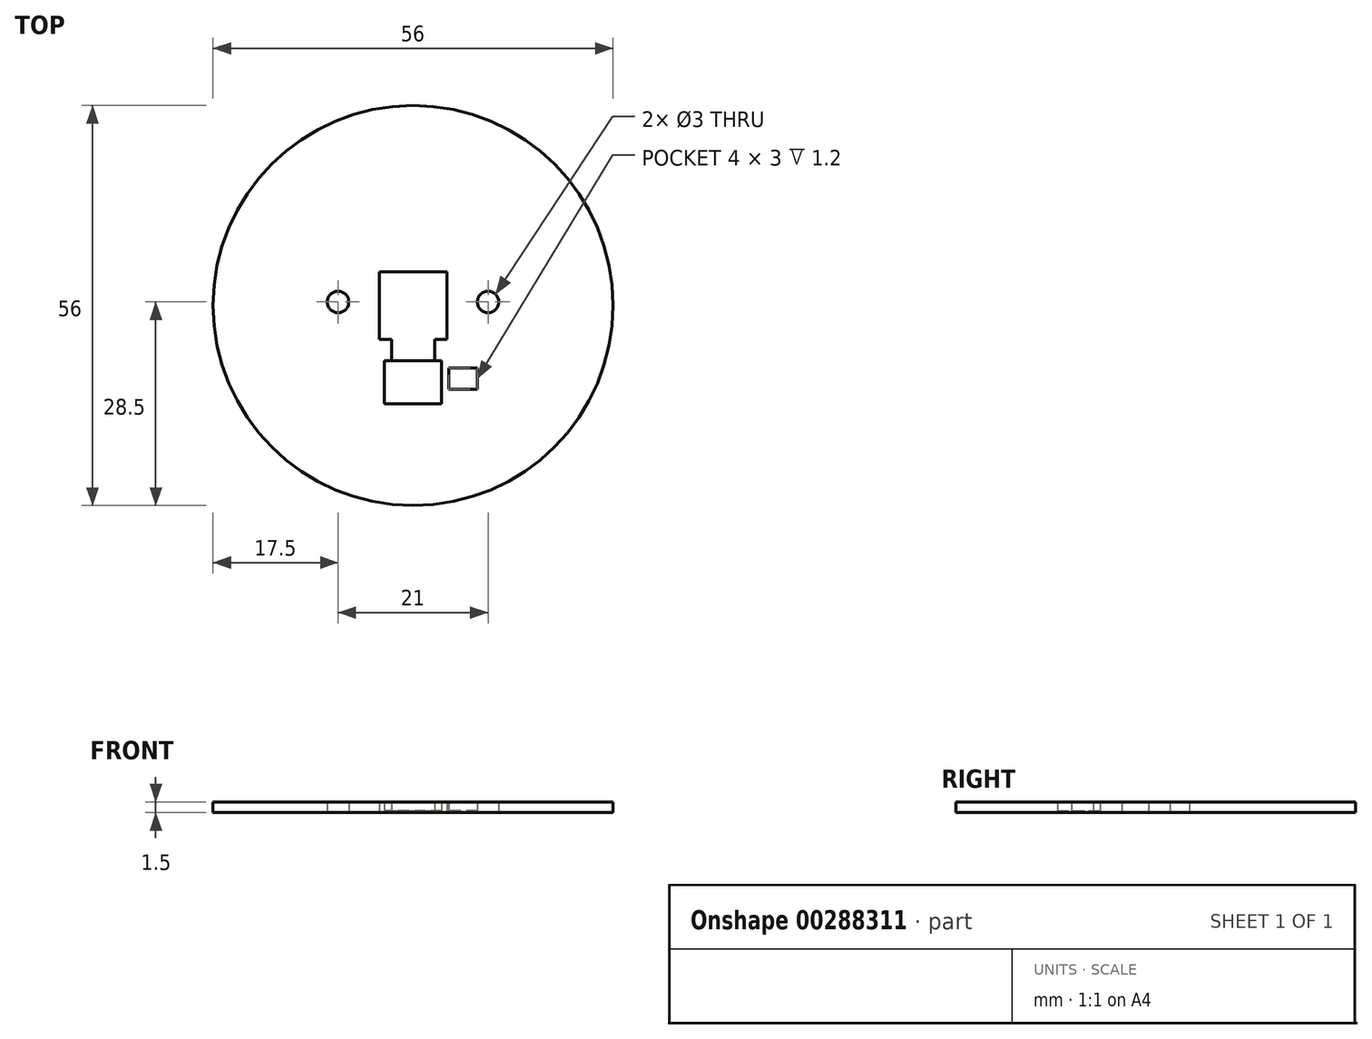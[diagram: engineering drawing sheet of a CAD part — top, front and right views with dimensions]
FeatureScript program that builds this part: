
annotation { "Feature Type Name" : "Feature", "Feature Type Description" : "" }
export const myFeature = defineFeature(function(context is Context, id is Id, definition is map)
    precondition{}
    {
        {
            var Q0;
            Q0=qCreatedBy(makeId("Top.planeOp"),FACE);
            var sketch = newSketch(context, id + "F0", { "sketchPlane" : qUnion([Q0])});
            skCircle(sketch, "E0", {"center": v(0, 0) * mm, "radius": 28 * mm});
            skPoint(sketch, "E1", {"position": v(-10.5, 0) * mm});
            skCircle(sketch, "E2", {"center": v(-10.5, 0.5) * mm, "radius": 1.5 * mm});
            skPoint(sketch, "E3", {"position": v(10.5, 0) * mm});
            skCircle(sketch, "E4", {"center": v(10.5, 0.5) * mm, "radius": 1.5 * mm});
            skLineSegment(sketch, "E5.bottom", {"start": v(-4.75, 4.75) * mm, "end": v(4.75, 4.75) * mm});
            skLineSegment(sketch, "E5.top", {"start": v(-4.75, -4.75) * mm, "end": v(4.75, -4.75) * mm});
            skLineSegment(sketch, "E5.left", {"start": v(-4.75, 4.75) * mm, "end": v(-4.75, -4.75) * mm});
            skLineSegment(sketch, "E5.right", {"start": v(4.75, 4.75) * mm, "end": v(4.75, -4.75) * mm});
            skLineSegment(sketch, "E6.bottom", {"start": v(-4, -7.75) * mm, "end": v(4, -7.75) * mm});
            skLineSegment(sketch, "E6.top", {"start": v(-4, -13.75) * mm, "end": v(4, -13.75) * mm});
            skLineSegment(sketch, "E6.left", {"start": v(-4, -7.75) * mm, "end": v(-4, -13.75) * mm});
            skLineSegment(sketch, "E6.right", {"start": v(4, -7.75) * mm, "end": v(4, -13.75) * mm});
            skLineSegment(sketch, "E7.bottom", {"start": v(-3, -4.75) * mm, "end": v(3, -4.75) * mm});
            skLineSegment(sketch, "E7.top", {"start": v(-3, -7.75) * mm, "end": v(3, -7.75) * mm});
            skLineSegment(sketch, "E7.left", {"start": v(-3, -4.75) * mm, "end": v(-3, -7.75) * mm});
            skLineSegment(sketch, "E7.right", {"start": v(3, -4.75) * mm, "end": v(3, -7.75) * mm});
            skLineSegment(sketch, "E8.bottom", {"start": v(5, -8.75) * mm, "end": v(9, -8.75) * mm});
            skLineSegment(sketch, "E8.top", {"start": v(5, -11.75) * mm, "end": v(9, -11.75) * mm});
            skLineSegment(sketch, "E8.left", {"start": v(5, -8.75) * mm, "end": v(5, -11.75) * mm});
            skLineSegment(sketch, "E8.right", {"start": v(9, -8.75) * mm, "end": v(9, -11.75) * mm});
            skSolve(sketch);
        }
        {
            var Q0;
            Q0=makeQuery(id+"F0.imprint","IMPRINT",FACE,{"disambiguationData":[TD([[makeQuery(id+"F0.imprint","IMPRINT",EDGE,{"derivedFrom":sQuery(id+"F0.wireOp",EDGE,"E0")}),1.0]])]});
            var Q1;
            Q1=makeQuery(id+"F0.imprint","IMPRINT",FACE,{"disambiguationData":[TD([[makeQuery(id+"F0.imprint","IMPRINT",EDGE,{"derivedFrom":sQuery(id+"F0.wireOp",EDGE,"E8.bottom")}),-1.0]])]});
            var Q2;
            Q2=makeQuery(id+"F0.imprint","IMPRINT",FACE,{"disambiguationData":[TD([[makeQuery(id+"F0.imprint","IMPRINT",EDGE,{"derivedFrom":sQuery(id+"F0.wireOp",EDGE,"E6.top")}),1.0]])]});
            var Q3;
            Q3=makeQuery(id+"F0.imprint","IMPRINT",FACE,{"disambiguationData":[TD([[makeQuery(id+"F0.imprint","IMPRINT",EDGE,{"derivedFrom":sQuery(id+"F0.wireOp",EDGE,"E7.bottom")}),-1.0]])]});
            extrude(context, id + "F1", {"entities" : qUnion([Q0, Q1, Q2, Q3]), "depth" : .3 * mm});
        }
        {
            var Q0;
            Q0=qSketchRegion(id+"F0",true);
            extrude(context, id + "F2", {"entities" : qUnion([Q0]), "operationType" : NewBodyOperationType.ADD, "depth" : 1.5 * mm});
        }
    });
